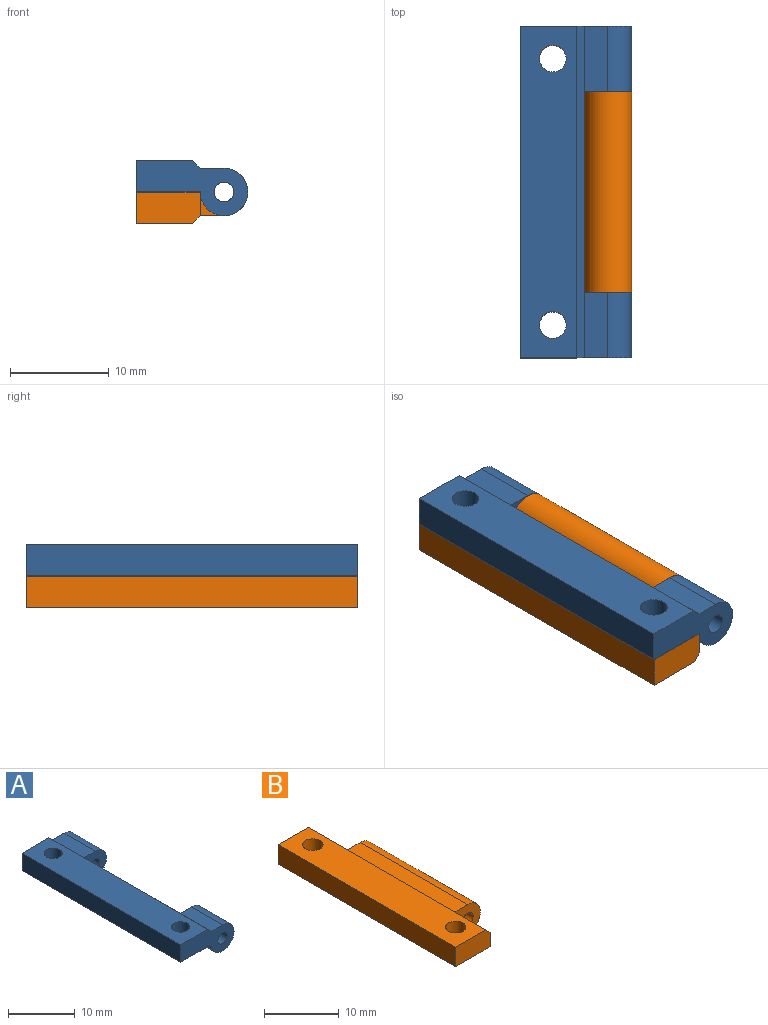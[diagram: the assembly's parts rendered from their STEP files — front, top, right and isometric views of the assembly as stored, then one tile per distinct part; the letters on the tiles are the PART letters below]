
ASSEMBLY  parts=2 mates=1
PART A: 17 faces, bbox 11.3x33.5x5.6 mm
  f0: cylinder r=1.35mm len=3.18mm, axis (0,0,-1), area 27mm2, adj f8,f11
  f1: cylinder r=1.35mm len=3.18mm, axis (0,0,-1), area 27mm2, adj f8,f11
  f2: cylinder r=1mm len=6.59mm, axis (0,-1,0), area 41.4mm2, adj f7,f10
  f3: cylinder r=2.4mm len=6.59mm, axis (0,-1,0), area 74.6mm2, adj f6,f9,f11,f15
  f4: cylinder r=1mm len=6.59mm, axis (0,-1,0), area 41.4mm2, adj f6,f9
  f5: cylinder r=2.4mm len=6.59mm, axis (0,-1,0), area 74.6mm2, adj f7,f10,f11,f14
  f6: plane 11.28x5.58mm, normal (0,1,0), area 36.5mm2, adj f3,f4,f8,f11,f12,f15,f16
  f7: plane 11.28x5.58mm, normal (0,-1,0), area 36.5mm2, adj f2,f5,f8,f11,f12,f14,f16
  f8: plane 33.53x5.7mm, normal (0,0,1), area 179.6mm2, adj f0,f1,f6,f7,f12,f16
  f9: plane 4.81x4.81mm, normal (0,-1,0), area 16.3mm2, adj f3,f4,f13,f15
  f10: plane 4.81x4.81mm, normal (0,1,0), area 16.3mm2, adj f2,f5,f13,f14
  f11: plane 33.53x6.47mm, normal (0,0,-1), area 205.4mm2, adj f0,f1,f3,f5,f6,f7,f12,f13
  f12: plane 33.53x3.18mm, normal (-1,0,0), area 106.5mm2, adj f6,f7,f8,f11
  f13: plane 20.35x2.4mm, normal (1,0,0), area 48.9mm2, adj f9,f10,f11,f16
  f14: plane 6.59x2.4mm, normal (0,0,1), area 15.8mm2, adj f5,f7,f10,f16
  f15: plane 6.59x2.4mm, normal (0,0,1), area 15.8mm2, adj f3,f6,f9,f16
  f16: plane 33.53x0.77mm, normal (0.71,0,0.71), area 36.5mm2, adj f6,f7,f8,f13,f14,f15
PART B: 15 faces, bbox 11.3x33.5x5.6 mm
  f0: cylinder r=1.35mm len=3.18mm, axis (0,0,-1), area 27mm2, adj f7,f9
  f1: cylinder r=1.35mm len=3.18mm, axis (0,0,-1), area 27mm2, adj f7,f9
  f2: cylinder r=1.03mm len=20.28mm, axis (0,-1,0), area 130.6mm2, adj f11,f12
  f3: cylinder r=2.4mm len=20.28mm, axis (0,-1,0), area 229.8mm2, adj f7,f11,f12,f13
  f4: plane 6.63x2.4mm, normal (1,0,0), area 15.9mm2, adj f5,f7,f11,f14
  f5: plane 6.47x3.18mm, normal (0,1,0), area 20.2mm2, adj f4,f7,f8,f9,f14
  f6: plane 6.47x3.18mm, normal (0,-1,0), area 20.2mm2, adj f7,f8,f9,f10,f14
  f7: plane 33.53x6.47mm, normal (0,0,-1), area 205.4mm2, adj f0,f1,f3,f4,f5,f6,f8,f10
  f8: plane 33.53x3.18mm, normal (-1,0,0), area 106.5mm2, adj f5,f6,f7,f9
  f9: plane 33.53x5.7mm, normal (0,0,1), area 179.6mm2, adj f0,f1,f5,f6,f8,f14
  f10: plane 6.63x2.4mm, normal (1,0,0), area 15.9mm2, adj f6,f7,f12,f14
  f11: plane 4.81x4.81mm, normal (0,1,0), area 16.1mm2, adj f2,f3,f4,f13
  f12: plane 4.81x4.81mm, normal (0,-1,0), area 16.1mm2, adj f2,f3,f10,f13
  f13: plane 20.28x2.4mm, normal (0,0,1), area 48.8mm2, adj f3,f11,f12,f14
  f14: plane 33.53x0.77mm, normal (0.71,0,0.71), area 36.5mm2, adj f4,f5,f6,f9,f10,f13
PLACE A t=(3.52,0.98,2.29)mm fixed
PLACE B rot(axis=(1,0,0),180deg) t=(3.52,34.47,2.29)mm
MATE revolute B.f2 <-> A.f2  axis (0,-1,0) through (3.52,7.57,2.29)mm
